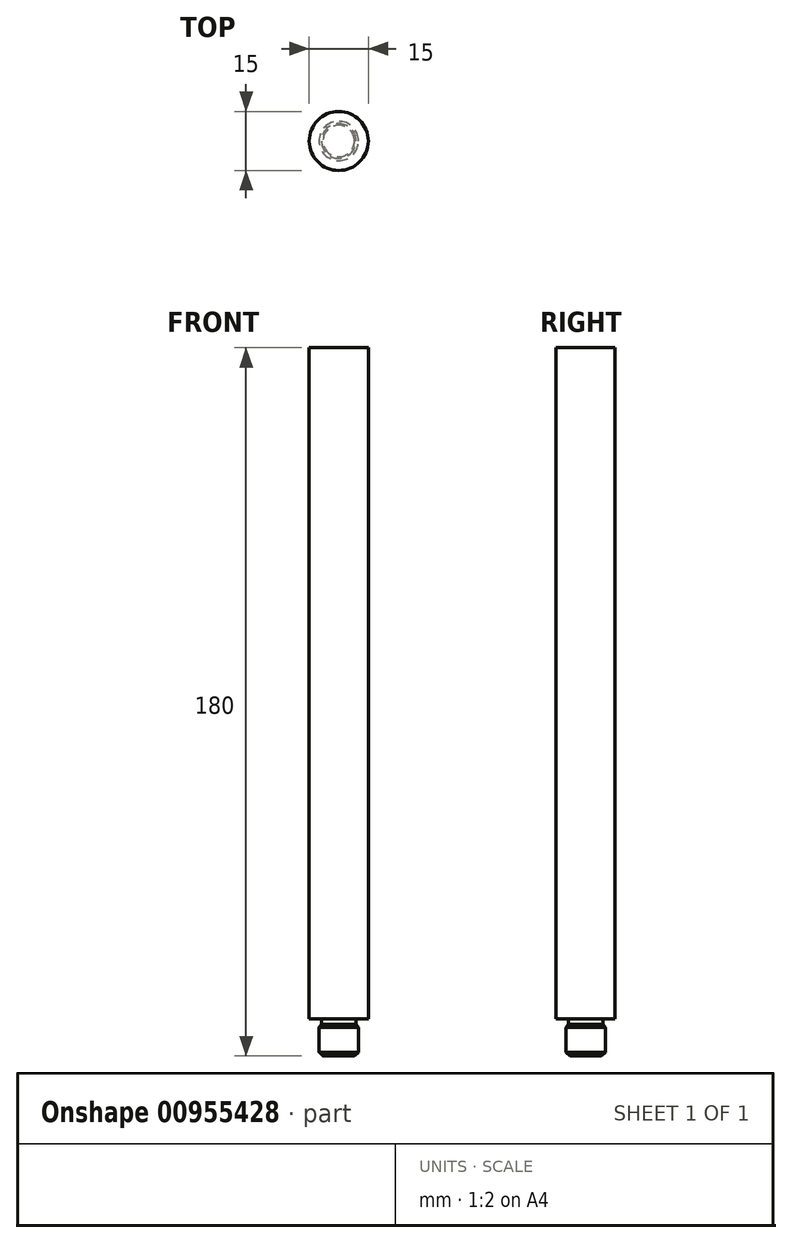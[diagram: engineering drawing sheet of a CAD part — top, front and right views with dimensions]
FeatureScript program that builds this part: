
annotation { "Feature Type Name" : "Feature", "Feature Type Description" : "" }
export const myFeature = defineFeature(function(context is Context, id is Id, definition is map)
    precondition{}
    {
        {
            var Q0;
            Q0=qCreatedBy(makeId("Top.planeOp"),FACE);
            var sketch = newSketch(context, id + "F0", { "sketchPlane" : qUnion([Q0])});
            skCircle(sketch, "E0", {"center": v(0, 0) * mm, "radius": 7.5 * mm});
            skSolve(sketch);
        }
        {
            var Q0;
            Q0=makeQuery(id+"F0.imprint","IMPRINT",FACE,{"disambiguationData":[TD([[makeQuery(id+"F0.imprint","IMPRINT",EDGE,{"derivedFrom":sQuery(id+"F0.wireOp",EDGE,"E0")}),1.0]])]});
            extrude(context, id + "F1", {"entities" : qUnion([Q0]), "depth" : 170.5 * mm, "offsetDistance" : 25 * mm});
        }
        {
            var Q0;
            Q0=makeQuery(id+"F1.opExtrude","CAP_FACE",FACE,{"disambiguationData":[OSD([sQuery(id+"F0.wireOp",EDGE,"E0")])],"isStart":true});
            var sketch = newSketch(context, id + "F2", { "sketchPlane" : qUnion([Q0])});
            skCircle(sketch, "E1", {"center": v(0, 0) * mm, "radius": 5 * mm});
            skSolve(sketch);
        }
        {
            var Q0;
            Q0=makeQuery(id+"F2.imprint","IMPRINT",FACE,{"disambiguationData":[TD([[makeQuery(id+"F2.imprint","IMPRINT",EDGE,{"derivedFrom":sQuery(id+"F2.wireOp",EDGE,"E1")}),1.0]])]});
            extrude(context, id + "F3", {"entities" : qUnion([Q0]), "operationType" : NewBodyOperationType.ADD, "depth" : 9.5 * mm, "offsetDistance" : 25 * mm});
        }
        {
            var Q0;
            Q0=makeQuery(id+"F3.opExtrude","CAP_EDGE",EDGE,{"disambiguationData":[OSD([sQuery(id+"F2.wireOp",EDGE,"E1")])],"isStart":false});
            chamfer(context, id + "F4", {"entities" : qUnion([Q0]), "width" : 1 * mm, "tangentPropagation" : true});
        }
        {
            var Q0;
            Q0=qCreatedBy(makeId("Front.planeOp"),FACE);
            var sketch = newSketch(context, id + "F5", { "sketchPlane" : qUnion([Q0])});
            skLineSegment(sketch, "E2", {"start": v(5.03, -2.22) * mm, "end": v(4.4, -1.4) * mm});
            skLineSegment(sketch, "E3", {"start": v(4.4, -1.4) * mm, "end": v(4.4, 0) * mm});
            skLineSegment(sketch, "E4", {"start": v(4.4, 0) * mm, "end": v(5.14, 0) * mm});
            skLineSegment(sketch, "E5", {"start": v(5.14, 0) * mm, "end": v(5.14, -2.22) * mm});
            skLineSegment(sketch, "E6", {"start": v(5.14, -2.22) * mm, "end": v(5.03, -2.22) * mm});
            skSolve(sketch);
        }
        {
            var Q0;
            Q0 = qSketchRegion(id + "F5", true);
            var Q1;
            Q1=makeQuery(id+"F3.opExtrude","SWEPT_FACE",FACE,{"disambiguationData":[OSD([sQuery(id+"F2.wireOp",EDGE,"E1")])]});
            revolve(context, id + "F6", {"operationType" : NewBodyOperationType.REMOVE, "surfaceOperationType" : NewSurfaceOperationType.NEW, "entities" : qUnion([Q0]), "axis" : qUnion([Q1]), "revolveType" : RevolveType.FULL, "oppositeDirection" : true});
        }
    });
